# Revit family: Shower-Base_Anti_Slip-KOHLER-UK-1.1824.032_1
name_source: partatom
category: Plumbing Fixtures
revit_build: Autodesk Revit 2017 (Build: 20160225_1515(x64)
units: mm (PartAtom-declared; Revit-internal decimal feet)

## family parameters
Cut with Voids When Loaded = No
Host = Face
OmniClass Number = 23.31.17.13
OmniClass Title = Shower Receptors
Part Type = Normal
Room Calculation Point = No
Round Connector Dimension = Use Diameter
Shared = No

## types (1)
- White
    ADA Compliant = No
    Assembly Code = D2010700
    CW Connection = No
    Cold Water Inlet = Cold Water Inlet
    Date Modified = 08/24/2021
    Default Elevation = 0"
    Description = LOW 800mm x 800mm Quad (Anti-Slip)
    Drain Included = Yes
    Finish = KOHLER-Acrylic-0-White
    Flow Rate = 0 GPM
    HW Connection = No
    Height = 1 9/16"
    Hot Water Inlet = Hot Water Inlet
    Length = 31 1/2"
    Manufacturer = KOHLER Co.
    Master Format 2014 = 22 42 23
    Master Format 2014 Name = Residential Showers
    Material = Acrylic
    Model = 1.1824.032.AS
    Pressure = 0.00 psi
    Product Name = UK
    Type = 1
    URL = https://www.kohler.co.uk
    Vent Connection = No
    Waste Connection = Yes
    Waste Water Outlet = Waste Water Outlet
    WaterSense Certified = No
    Width = 31 1/2"

## geometry (parser evidence)
native form markers: Sweep x3
no freeform markers — native parametric forms only
